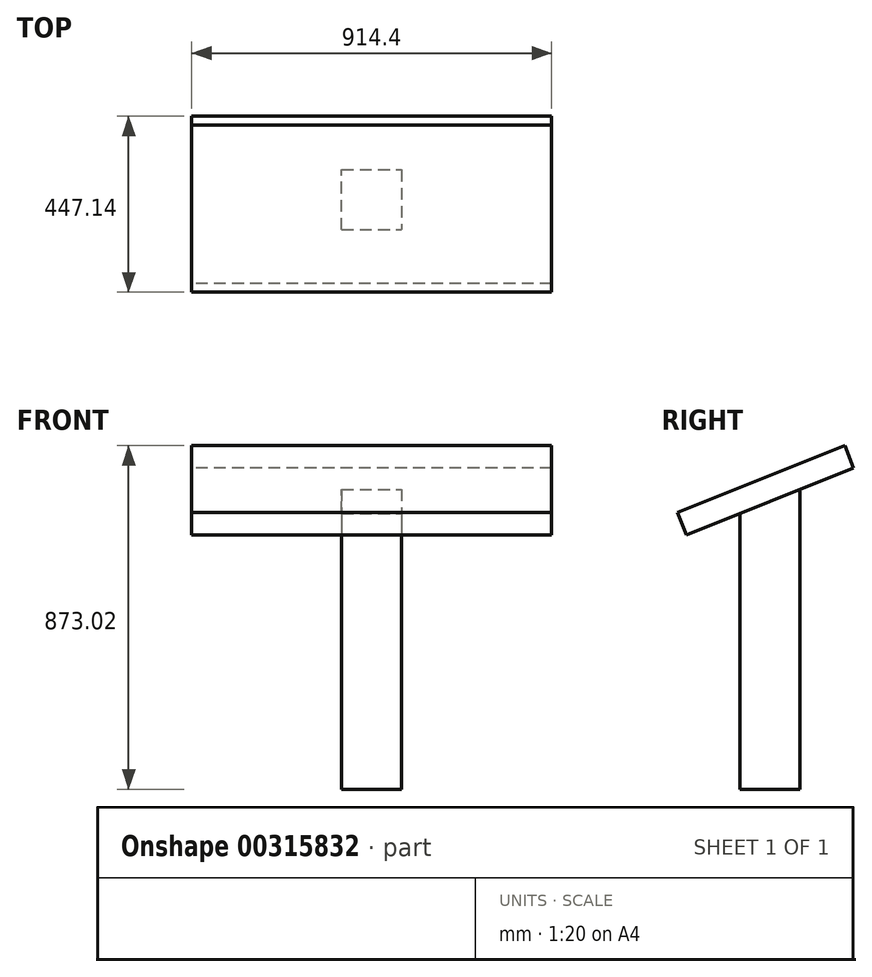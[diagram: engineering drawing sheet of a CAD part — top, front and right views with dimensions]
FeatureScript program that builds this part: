
annotation { "Feature Type Name" : "Feature", "Feature Type Description" : "" }
export const myFeature = defineFeature(function(context is Context, id is Id, definition is map)
    precondition{}
    {
        {
            var Q0;
            Q0=qCreatedBy(makeId("Top.planeOp"),FACE);
            var sketch = newSketch(context, id + "F0", { "sketchPlane" : qUnion([Q0])});
            skLineSegment(sketch, "E0.bottom", {"start": v(-69.05, -88.12) * mm, "end": v(83.35, -88.12) * mm});
            skLineSegment(sketch, "E0.top", {"start": v(-69.05, 64.28) * mm, "end": v(83.35, 64.28) * mm});
            skLineSegment(sketch, "E0.left", {"start": v(-69.05, -88.12) * mm, "end": v(-69.05, 64.28) * mm});
            skLineSegment(sketch, "E0.right", {"start": v(83.35, -88.12) * mm, "end": v(83.35, 64.28) * mm});
            skSolve(sketch);
        }
        {
            var Q0;
            Q0=makeQuery(id+"F0.imprint","IMPRINT",FACE,{"disambiguationData":[TD([[makeQuery(id+"F0.imprint","IMPRINT",EDGE,{"derivedFrom":sQuery(id+"F0.wireOp",EDGE,"E0.bottom")}),1.0]])]});
            extrude(context, id + "F1", {"entities" : qUnion([Q0]), "depth" : 762 * mm});
        }
        {
            var Q0;
            Q0=makeQuery(id+"F1.opExtrude","SWEPT_FACE",FACE,{"disambiguationData":[OSD([sQuery(id+"F0.wireOp",EDGE,"E0.right")])]});
            var sketch = newSketch(context, id + "F2", { "sketchPlane" : qUnion([Q0])});
            skLineSegment(sketch, "E1", {"start": v(-88.12, 762) * mm, "end": v(-88.12, 701.04) * mm});
            skLineSegment(sketch, "E2", {"start": v(64.28, 762) * mm, "end": v(-88.12, 701.04) * mm});
            skSolve(sketch);
        }
        {
            var Q0;
            Q0=makeQuery(id+"F2.imprint","IMPRINT",FACE,{"disambiguationData":[TD([[makeQuery(id+"F2.imprint","IMPRINT",EDGE,{"derivedFrom":sQuery(id+"F2.wireOp",EDGE,"E1")}),1.0]])]});
            extrude(context, id + "F3", {"entities" : qUnion([Q0]), "operationType" : NewBodyOperationType.REMOVE, "endBound" : BoundingType.THROUGH_ALL, "oppositeDirection" : true, "depth" : 30.48 * mm});
        }
        {
            var Q0;
            Q0=makeQuery(id+"F3.boolean.opBoolean","COPY",FACE,{"derivedFrom":makeQuery(id+"F3.opExtrude","SWEPT_FACE",FACE,{"disambiguationData":[OSD([sQuery(id+"F2.wireOp",EDGE,"E2")])]})});
            var sketch = newSketch(context, id + "F4", { "sketchPlane" : qUnion([Q0])});
            skLineSegment(sketch, "E3.bottom", {"start": v(464.35, 32.01) * mm, "end": v(-450.05, 32.01) * mm});
            skLineSegment(sketch, "E3.top", {"start": v(464.35, 489.21) * mm, "end": v(-450.05, 489.21) * mm});
            skLineSegment(sketch, "E3.left", {"start": v(464.35, 32.01) * mm, "end": v(464.35, 489.21) * mm});
            skLineSegment(sketch, "E3.right", {"start": v(-450.05, 32.01) * mm, "end": v(-450.05, 489.21) * mm});
            skPoint(sketch, "E3.middle", {"position": v(7.15, 260.61) * mm});
            skPoint(sketch, "E3.middle.positionSnap0", {"position": v(7.15, 342.68) * mm});
            skPoint(sketch, "E3.middle.positionSnap1", {"position": v(83.35, 260.61) * mm});
            skPoint(sketch, "E3.centerSnap0", {"position": v(7.15, 342.68) * mm});
            skPoint(sketch, "E3.centerSnap1", {"position": v(83.35, 260.61) * mm});
            skSolve(sketch);
        }
        {
            var Q0;
            Q0 = qSketchRegion(id + "F4", true);
            extrude(context, id + "F5", {"entities" : qUnion([Q0]), "operationType" : NewBodyOperationType.ADD, "depth" : 60.96 * mm});
        }
    });
